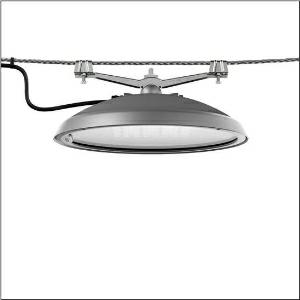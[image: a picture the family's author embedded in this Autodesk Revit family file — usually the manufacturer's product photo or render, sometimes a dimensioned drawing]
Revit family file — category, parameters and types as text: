
# Revit family: dl_r__50_iq_mini___st0_8s_5xa248v41f08ge_d665
name_source: partatom
category: Lighting Fixtures
units: mm (PartAtom-declared; Revit-internal decimal feet)

## family parameters
Cut with Voids When Loaded = No
Host = Face
Light Source = No
Part Type = Normal
Room Calculation Point = No
Round Connector Dimension = Use Diameter
Shared = No

## types (1)
- --- (1 x LED, 5190 lm, 31.2 W, 4000K)
    Apparent Load = 31 VA
    CIE Flux Codes = 38 75 97 100 100
    Color Rendering = 70
    Color Temperature = 4000K
    Default Elevation = 1800 mm
    Description = DL® 50 iQ mini, catenary luminaire, primary light control with lens, of PMMA, primary optical cover: cover, of toughened safety glass, transparent, light distribution: ST0.8s, light emission: direct distribution, primary light characteristic: symmetric, installation type: suspended mounting, LED, High Power LED, rated luminous flux: 5.190lm, luminous efficacy: 166lm/W, light colour: 740, colour temperature: 4000K, control gear: iQ Street-Remote, control: optimised constant luminous flux control (CLO 2.0), Desk-Remote (wireless, voltage-free reading and setting of iQ features in the workshop via application-optimized NFC function/RFID function), Light-Fading, Smart-Wire, Night-Set, Lumen-Switch, Temp-Guard, Auto-Match, Street-Remote, mains connection: 230..240V, AC, 50/60Hz, start of lifetime: 31W, end of service life: 32W, reduction: 15W, luminaire housing, of diecast aluminium, powder-coated, Siteco® metallic grey (DB 702S), diameter: 500mm, height: 115mm, mounting height: 4..12m, protection rating (complete): IP66, insulation class (complete): insulation class II (safety insulation), certification: CE, ENEC, ENEC+, VDE, impact resistance: IK08, permissible operating ambient temperature for outdoor applications: -25..+40°C, standard-compliant lighting for roads and squares, packaging unit: 1 piece

Light Distribution: ST0.8s
    Height = 124 mm
    Lamp = 1 x LED
    Lamp Light Flux = 5190 lm
    Lamp Power = 31.2 W
    Lamp count = 1
    Length = 500 mm
    Luminous efficacy = 166 lm/W
    Manufacturer = Siteco
    ModVariant = No
    Model = 5XA248V41F08GE
    Number of Poles = 1
    OnlyDefault = Yes
    Power Factor = 1
    Product Name = DL® 50 iQ mini | ST0.8s
    Product group = catenary luminaire
    ProductGroupID = 6300
    Protection Class = Protection class II
    Protection Degree = IP 66
    RLX_Detail_Level = 1
    RLX_Emergency_Light_Flux = 0 lm
    RLX_Emergency_Type = 0
    RLX_Emergency_Type_DB = No
    RlxData = <blob elided: 123781 chars, md5=76a37874>
    Socket = socket
    Standby Power = 0 W
    System Light Flux = 5190 lm
    System Power = 31 W
    Type Comments = factory setting: luminous flux: 100 % | dim-lin: 254 | 325 mA
    Type Image = l_1242791.jpg
    URL = http://relux.com
    VarID = @adj_162575
    Voltage = 0 V
    Weight = 0.00 kg
    Width = 0 mm  [stored 0 ft]

note: [stored X ft] marks values corroborated as IEEE doubles in the binary element streams (Revit-internal decimal feet)

## geometry (parser evidence)
native form markers: Blend x4, Sweep x11
no freeform markers — native parametric forms only
